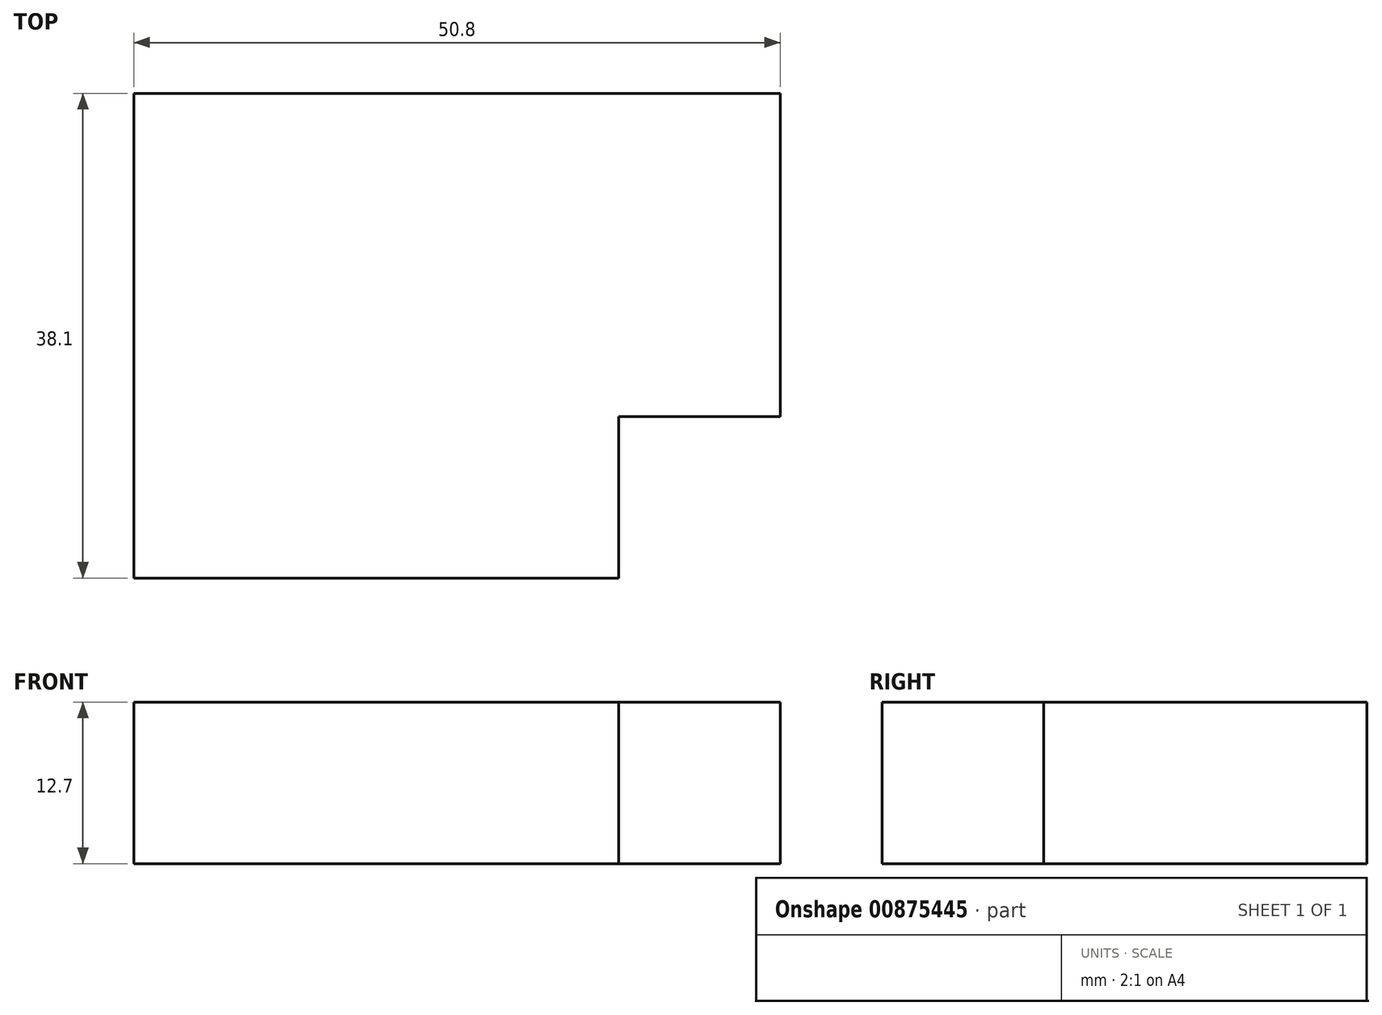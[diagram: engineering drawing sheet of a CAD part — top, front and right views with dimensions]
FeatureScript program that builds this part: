
annotation { "Feature Type Name" : "Feature", "Feature Type Description" : "" }
export const myFeature = defineFeature(function(context is Context, id is Id, definition is map)
    precondition{}
    {
        {
            var Q0;
            Q0=qCreatedBy(makeId("Top.planeOp"),FACE);
            var sketch = newSketch(context, id + "F0", { "sketchPlane" : qUnion([Q0])});
            skLineSegment(sketch, "E0.top", {"start": v(25.4, 19.05) * mm, "end": v(-25.4, 19.05) * mm});
            skLineSegment(sketch, "E0.right", {"start": v(-25.4, -19.05) * mm, "end": v(-25.4, 19.05) * mm});
            skPoint(sketch, "E0.middle", {"position": v(0, 0) * mm});
            skLineSegment(sketch, "E1.top", {"start": v(25.4, -6.35) * mm, "end": v(12.7, -6.35) * mm});
            skLineSegment(sketch, "E1.right", {"start": v(12.7, -19.05) * mm, "end": v(12.7, -6.35) * mm});
            skLineSegment(sketch, "E2", {"start": v(-25.4, -19.05) * mm, "end": v(12.7, -19.05) * mm});
            skLineSegment(sketch, "E3", {"start": v(25.4, 19.05) * mm, "end": v(25.4, -6.35) * mm});
            skSolve(sketch);
        }
        {
            var Q0;
            Q0 = qSketchRegion(id + "F0", true);
            extrude(context, id + "F1", {"entities" : qUnion([Q0]), "depth" : 12.7 * mm, "offsetDistance" : 25.4 * mm});
        }
    });
